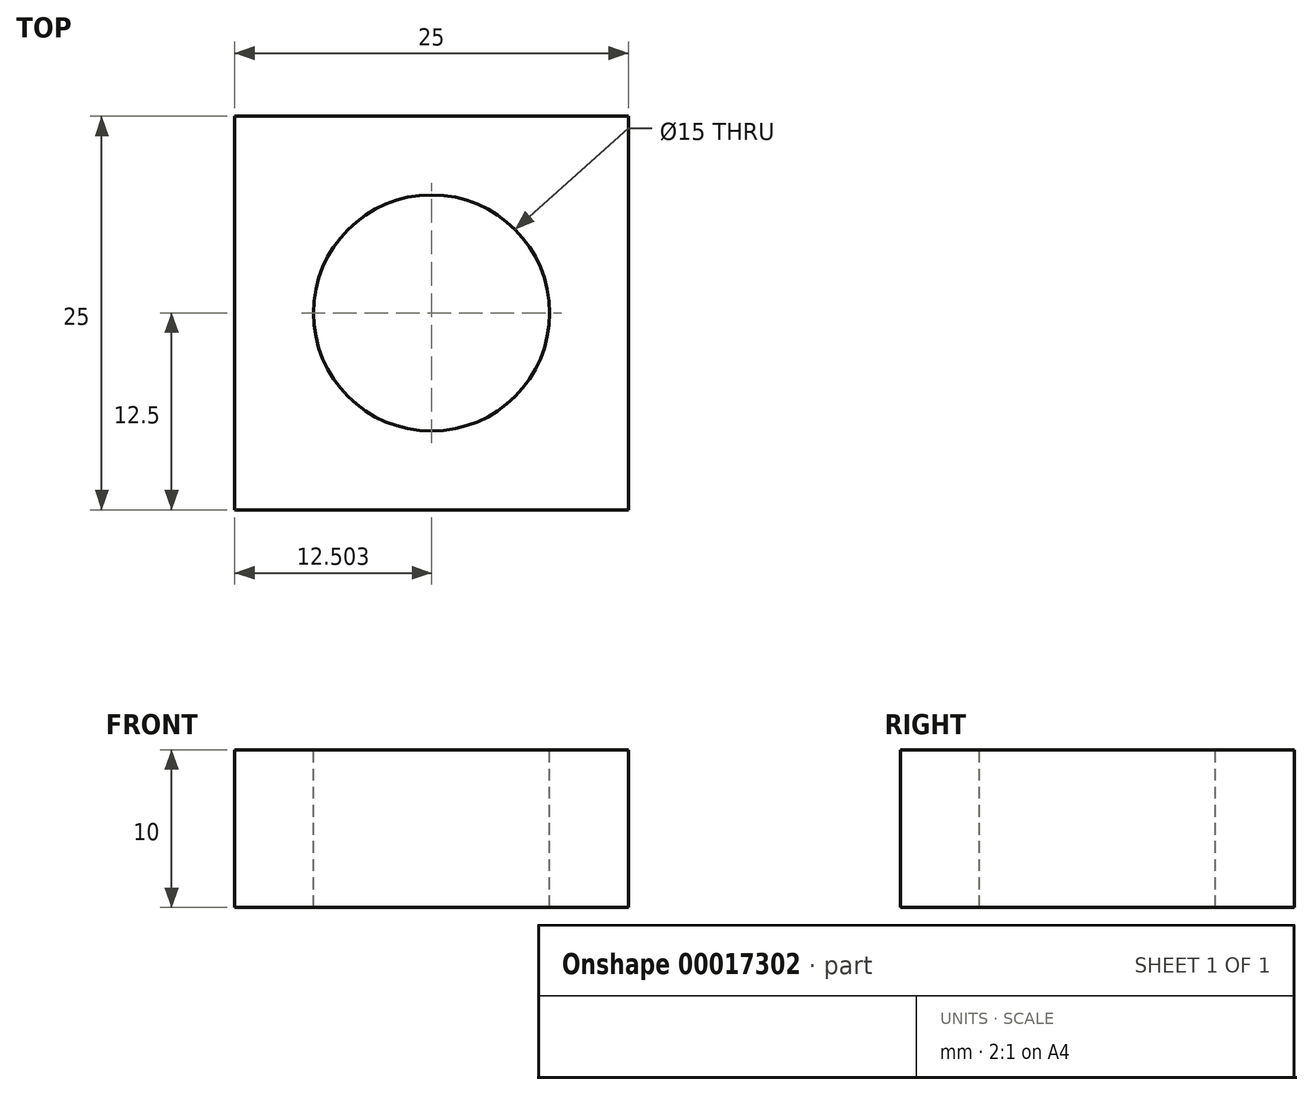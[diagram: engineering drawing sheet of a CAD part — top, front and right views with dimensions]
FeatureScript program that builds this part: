
annotation { "Feature Type Name" : "Feature", "Feature Type Description" : "" }
export const myFeature = defineFeature(function(context is Context, id is Id, definition is map)
    precondition{}
    {
        {
            var Q0;
            Q0=qCreatedBy(makeId("Front.planeOp"),FACE);
            var sketch = newSketch(context, id + "F0", { "sketchPlane" : qUnion([Q0])});
            skLineSegment(sketch, "E0.bottom", {"start": v(-8.63, 2.12) * mm, "end": v(16.37, 2.12) * mm});
            skLineSegment(sketch, "E0.top", {"start": v(-8.63, -7.88) * mm, "end": v(16.37, -7.88) * mm});
            skLineSegment(sketch, "E0.left", {"start": v(-8.63, 2.12) * mm, "end": v(-8.63, -7.88) * mm});
            skLineSegment(sketch, "E0.right", {"start": v(16.37, 2.12) * mm, "end": v(16.37, -7.88) * mm});
            skSolve(sketch);
        }
        {
            var Q0;
            Q0 = qSketchRegion(id + "F0", true);
            extrude(context, id + "F1", {"entities" : qUnion([Q0]), "depth" : 25 * mm});
        }
        {
            var Q0;
            Q0=makeQuery(id+"F1.opExtrude","SWEPT_FACE",FACE,{"disambiguationData":[OSD([sQuery(id+"F0.wireOp",EDGE,"E0.bottom")])]});
            var sketch = newSketch(context, id + "F2", { "sketchPlane" : qUnion([Q0])});
            skCircle(sketch, "E1", {"center": v(3.87, -12.5) * mm, "radius": 7.5 * mm});
            skSolve(sketch);
        }
        {
            var Q0;
            Q0=makeQuery(id+"F2.imprint","IMPRINT",FACE,{"disambiguationData":[TD([[makeQuery(id+"F2.imprint","IMPRINT",EDGE,{"derivedFrom":sQuery(id+"F2.wireOp",EDGE,"E1")}),1.0]])]});
            extrude(context, id + "F3", {"entities" : qUnion([Q0]), "operationType" : NewBodyOperationType.REMOVE, "oppositeDirection" : true, "depth" : 25 * mm});
        }
    });
